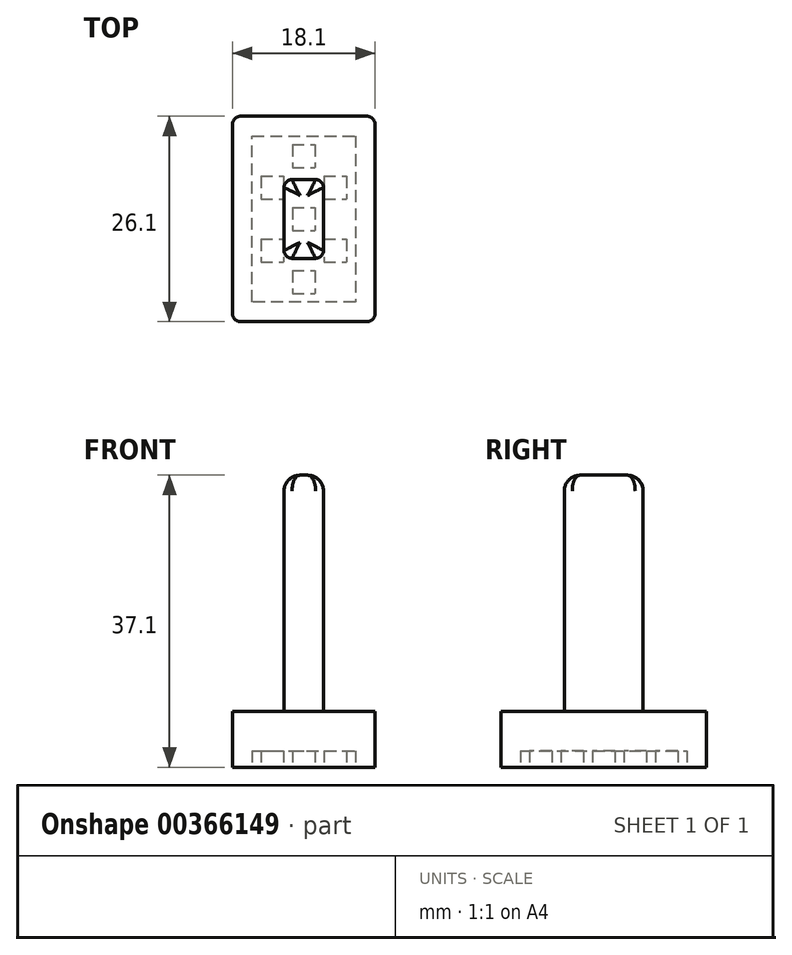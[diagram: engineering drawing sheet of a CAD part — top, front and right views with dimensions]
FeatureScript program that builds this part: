
annotation { "Feature Type Name" : "Feature", "Feature Type Description" : "" }
export const myFeature = defineFeature(function(context is Context, id is Id, definition is map)
    precondition{}
    {
        {
            var Q0;
            Q0=qCreatedBy(makeId("Top.planeOp"),FACE);
            var sketch = newSketch(context, id + "F0", { "sketchPlane" : qUnion([Q0])});
            skCircle(sketch, "E0", {"center": v(0, 0) * mm, "radius": 2.45 * mm});
            skCircle(sketch, "E1", {"center": v(0, -8) * mm, "radius": 2.45 * mm});
            skCircle(sketch, "E2", {"center": v(8, 0) * mm, "radius": 2.45 * mm});
            skCircle(sketch, "E3", {"center": v(8, -8) * mm, "radius": 2.45 * mm});
            skCircle(sketch, "E4", {"center": v(0, -16) * mm, "radius": 2.45 * mm});
            skCircle(sketch, "E5", {"center": v(8, -16) * mm, "radius": 2.45 * mm});
            skLineSegment(sketch, "E6", {"start": v(-2.55, 2.55) * mm, "end": v(10.55, 2.55) * mm});
            skLineSegment(sketch, "E7", {"start": v(10.55, 2.55) * mm, "end": v(10.55, -18.55) * mm});
            skLineSegment(sketch, "E8", {"start": v(10.55, -18.55) * mm, "end": v(-2.55, -18.55) * mm});
            skLineSegment(sketch, "E9", {"start": v(-2.55, -18.55) * mm, "end": v(-2.55, 2.55) * mm});
            skLineSegment(sketch, "E10.bottom", {"start": v(2.55, 1.45) * mm, "end": v(5.45, 1.45) * mm});
            skLineSegment(sketch, "E10.top", {"start": v(2.55, -1.45) * mm, "end": v(5.45, -1.45) * mm});
            skLineSegment(sketch, "E10.left", {"start": v(2.55, 1.45) * mm, "end": v(2.55, -1.45) * mm});
            skLineSegment(sketch, "E10.right", {"start": v(5.45, 1.45) * mm, "end": v(5.45, -1.45) * mm});
            skLineSegment(sketch, "E11.bottom", {"start": v(-1.45, -2.55) * mm, "end": v(1.45, -2.55) * mm});
            skLineSegment(sketch, "E11.top", {"start": v(-1.45, -5.45) * mm, "end": v(1.45, -5.45) * mm});
            skLineSegment(sketch, "E11.left", {"start": v(-1.45, -2.55) * mm, "end": v(-1.45, -5.45) * mm});
            skLineSegment(sketch, "E11.right", {"start": v(1.45, -2.55) * mm, "end": v(1.45, -5.45) * mm});
            skLineSegment(sketch, "E12.bottom", {"start": v(6.55, -2.55) * mm, "end": v(9.45, -2.55) * mm});
            skLineSegment(sketch, "E12.top", {"start": v(6.55, -5.45) * mm, "end": v(9.45, -5.45) * mm});
            skLineSegment(sketch, "E12.left", {"start": v(6.55, -2.55) * mm, "end": v(6.55, -5.45) * mm});
            skLineSegment(sketch, "E12.right", {"start": v(9.45, -2.55) * mm, "end": v(9.45, -5.45) * mm});
            skLineSegment(sketch, "E13.bottom", {"start": v(-1.45, -10.55) * mm, "end": v(1.45, -10.55) * mm});
            skLineSegment(sketch, "E13.top", {"start": v(-1.45, -13.45) * mm, "end": v(1.45, -13.45) * mm});
            skLineSegment(sketch, "E13.left", {"start": v(-1.45, -10.55) * mm, "end": v(-1.45, -13.45) * mm});
            skLineSegment(sketch, "E13.right", {"start": v(1.45, -10.55) * mm, "end": v(1.45, -13.45) * mm});
            skLineSegment(sketch, "E14.bottom", {"start": v(6.55, -10.55) * mm, "end": v(9.45, -10.55) * mm});
            skLineSegment(sketch, "E14.top", {"start": v(6.55, -13.45) * mm, "end": v(9.45, -13.45) * mm});
            skLineSegment(sketch, "E14.left", {"start": v(6.55, -10.55) * mm, "end": v(6.55, -13.45) * mm});
            skLineSegment(sketch, "E14.right", {"start": v(9.45, -10.55) * mm, "end": v(9.45, -13.45) * mm});
            skLineSegment(sketch, "E15.bottom", {"start": v(2.55, -14.55) * mm, "end": v(5.45, -14.55) * mm});
            skLineSegment(sketch, "E15.top", {"start": v(2.55, -17.45) * mm, "end": v(5.45, -17.45) * mm});
            skLineSegment(sketch, "E15.left", {"start": v(2.55, -14.55) * mm, "end": v(2.55, -17.45) * mm});
            skLineSegment(sketch, "E15.right", {"start": v(5.45, -14.55) * mm, "end": v(5.45, -17.45) * mm});
            skLineSegment(sketch, "E16.0", {"start": v(-5.05, 5.05) * mm, "end": v(13.05, 5.05) * mm});
            skLineSegment(sketch, "E17.0", {"start": v(-5.05, -21.05) * mm, "end": v(-5.05, 5.05) * mm});
            skLineSegment(sketch, "E18.0", {"start": v(13.05, 5.05) * mm, "end": v(13.05, -21.05) * mm});
            skLineSegment(sketch, "E19.0", {"start": v(13.05, -21.05) * mm, "end": v(-5.05, -21.05) * mm});
            skLineSegment(sketch, "E20.bottom", {"start": v(2.55, -6.55) * mm, "end": v(5.45, -6.55) * mm});
            skLineSegment(sketch, "E20.top", {"start": v(2.55, -9.45) * mm, "end": v(5.45, -9.45) * mm});
            skLineSegment(sketch, "E20.left", {"start": v(2.55, -6.55) * mm, "end": v(2.55, -9.45) * mm});
            skLineSegment(sketch, "E20.right", {"start": v(5.45, -6.55) * mm, "end": v(5.45, -9.45) * mm});
            skSolve(sketch);
        }
        {
            var Q0;
            Q0 = qSketchRegion(id + "F0", true);
            var Q1;
            Q1=makeQuery(id+"F0.imprint","IMPRINT",FACE,{"disambiguationData":[TD([[makeQuery(id+"F0.imprint","IMPRINT",EDGE,{"derivedFrom":sQuery(id+"F0.wireOp",EDGE,"E10.bottom")}),-1.0]])]});
            var Q2;
            Q2=makeQuery(id+"F0.imprint","IMPRINT",FACE,{"disambiguationData":[TD([[makeQuery(id+"F0.imprint","IMPRINT",EDGE,{"derivedFrom":sQuery(id+"F0.wireOp",EDGE,"E11.bottom")}),-1.0]])]});
            var Q3;
            Q3=makeQuery(id+"F0.imprint","IMPRINT",FACE,{"disambiguationData":[TD([[makeQuery(id+"F0.imprint","IMPRINT",EDGE,{"derivedFrom":sQuery(id+"F0.wireOp",EDGE,"E12.bottom")}),-1.0]])]});
            var Q4;
            Q4=makeQuery(id+"F0.imprint","IMPRINT",FACE,{"disambiguationData":[TD([[makeQuery(id+"F0.imprint","IMPRINT",EDGE,{"derivedFrom":sQuery(id+"F0.wireOp",EDGE,"E20.bottom")}),-1.0]])]});
            var Q5;
            Q5=makeQuery(id+"F0.imprint","IMPRINT",FACE,{"disambiguationData":[TD([[makeQuery(id+"F0.imprint","IMPRINT",EDGE,{"derivedFrom":sQuery(id+"F0.wireOp",EDGE,"E14.bottom")}),-1.0]])]});
            var Q6;
            Q6=makeQuery(id+"F0.imprint","IMPRINT",FACE,{"disambiguationData":[TD([[makeQuery(id+"F0.imprint","IMPRINT",EDGE,{"derivedFrom":sQuery(id+"F0.wireOp",EDGE,"E13.bottom")}),-1.0]])]});
            var Q7;
            Q7=makeQuery(id+"F0.imprint","IMPRINT",FACE,{"disambiguationData":[TD([[makeQuery(id+"F0.imprint","IMPRINT",EDGE,{"derivedFrom":sQuery(id+"F0.wireOp",EDGE,"E15.bottom")}),-1.0]])]});
            extrude(context, id + "F1", {"entities" : qUnion([Q0, Q1, Q2, Q3, Q4, Q5, Q6, Q7]), "depth" : 2.1 * mm});
        }
        {
            var Q0;
            Q0=makeQuery(id+"F1.opExtrude","CAP_FACE",FACE,{"disambiguationData":[OSD([sQuery(id+"F0.wireOp",EDGE,"E6"),sQuery(id+"F0.wireOp",EDGE,"E7"),sQuery(id+"F0.wireOp",EDGE,"E8"),sQuery(id+"F0.wireOp",EDGE,"E9"),sQuery(id+"F0.wireOp",EDGE,"E16.0"),sQuery(id+"F0.wireOp",EDGE,"E17.0"),sQuery(id+"F0.wireOp",EDGE,"E18.0"),sQuery(id+"F0.wireOp",EDGE,"E19.0")])],"isStart":false});
            var sketch = newSketch(context, id + "F2", { "sketchPlane" : qUnion([Q0])});
            skLineSegment(sketch, "E21.bottom", {"start": v(-5.05, 5.05) * mm, "end": v(13.05, 5.05) * mm});
            skLineSegment(sketch, "E21.top", {"start": v(-5.05, -21.05) * mm, "end": v(13.05, -21.05) * mm});
            skLineSegment(sketch, "E21.left", {"start": v(-5.05, 5.05) * mm, "end": v(-5.05, -21.05) * mm});
            skLineSegment(sketch, "E21.right", {"start": v(13.05, 5.05) * mm, "end": v(13.05, -21.05) * mm});
            skSolve(sketch);
        }
        {
            var Q0;
            Q0 = qSketchRegion(id + "F2", true);
            extrude(context, id + "F3", {"entities" : qUnion([Q0]), "depth" : 5 * mm});
        }
        {
            var Q0;
            Q0=makeQuery(id+"F3.opExtrude","SWEPT_BODY",BODY,{"disambiguationData":[OSD([sQuery(id+"F2.wireOp",EDGE,"E21.bottom"),sQuery(id+"F2.wireOp",EDGE,"E21.top"),sQuery(id+"F2.wireOp",EDGE,"E21.left"),sQuery(id+"F2.wireOp",EDGE,"E21.right")])]});
            var Q1;
            Q1=makeQuery(id+"F1.opExtrude","SWEPT_BODY",BODY,{"disambiguationData":[OSD([sQuery(id+"F0.wireOp",EDGE,"E15.bottom"),sQuery(id+"F0.wireOp",EDGE,"E15.top"),sQuery(id+"F0.wireOp",EDGE,"E15.left"),sQuery(id+"F0.wireOp",EDGE,"E15.right")])]});
            var Q2;
            Q2=makeQuery(id+"F1.opExtrude","SWEPT_BODY",BODY,{"disambiguationData":[OSD([sQuery(id+"F0.wireOp",EDGE,"E6"),sQuery(id+"F0.wireOp",EDGE,"E7"),sQuery(id+"F0.wireOp",EDGE,"E8"),sQuery(id+"F0.wireOp",EDGE,"E9"),sQuery(id+"F0.wireOp",EDGE,"E16.0"),sQuery(id+"F0.wireOp",EDGE,"E17.0"),sQuery(id+"F0.wireOp",EDGE,"E18.0"),sQuery(id+"F0.wireOp",EDGE,"E19.0")])]});
            var Q3;
            Q3=makeQuery(id+"F1.opExtrude","SWEPT_BODY",BODY,{"disambiguationData":[OSD([sQuery(id+"F0.wireOp",EDGE,"E12.bottom"),sQuery(id+"F0.wireOp",EDGE,"E12.top"),sQuery(id+"F0.wireOp",EDGE,"E12.left"),sQuery(id+"F0.wireOp",EDGE,"E12.right")])]});
            var Q4;
            Q4=makeQuery(id+"F1.opExtrude","SWEPT_BODY",BODY,{"disambiguationData":[OSD([sQuery(id+"F0.wireOp",EDGE,"E13.bottom"),sQuery(id+"F0.wireOp",EDGE,"E13.top"),sQuery(id+"F0.wireOp",EDGE,"E13.left"),sQuery(id+"F0.wireOp",EDGE,"E13.right")])]});
            var Q5;
            Q5=makeQuery(id+"F1.opExtrude","SWEPT_BODY",BODY,{"disambiguationData":[OSD([sQuery(id+"F0.wireOp",EDGE,"E10.bottom"),sQuery(id+"F0.wireOp",EDGE,"E10.top"),sQuery(id+"F0.wireOp",EDGE,"E10.left"),sQuery(id+"F0.wireOp",EDGE,"E10.right")])]});
            var Q6;
            Q6=makeQuery(id+"F1.opExtrude","SWEPT_BODY",BODY,{"disambiguationData":[OSD([sQuery(id+"F0.wireOp",EDGE,"E14.bottom"),sQuery(id+"F0.wireOp",EDGE,"E14.top"),sQuery(id+"F0.wireOp",EDGE,"E14.left"),sQuery(id+"F0.wireOp",EDGE,"E14.right")])]});
            var Q7;
            Q7=makeQuery(id+"F1.opExtrude","SWEPT_BODY",BODY,{"disambiguationData":[OSD([sQuery(id+"F0.wireOp",EDGE,"E11.bottom"),sQuery(id+"F0.wireOp",EDGE,"E11.top"),sQuery(id+"F0.wireOp",EDGE,"E11.left"),sQuery(id+"F0.wireOp",EDGE,"E11.right")])]});
            var Q8;
            Q8=makeQuery(id+"F1.opExtrude","SWEPT_BODY",BODY,{"disambiguationData":[OSD([sQuery(id+"F0.wireOp",EDGE,"E20.bottom"),sQuery(id+"F0.wireOp",EDGE,"E20.top"),sQuery(id+"F0.wireOp",EDGE,"E20.left"),sQuery(id+"F0.wireOp",EDGE,"E20.right")])]});
            booleanBodies(context, id + "F4", {"operationType" : BooleanOperationType.UNION, "tools" : qUnion([Q0, Q1, Q2, Q3, Q4, Q5, Q6, Q7, Q8])});
        }
        {
            var Q0;
            Q0=makeQuery(id+"F3.opExtrude","CAP_FACE",FACE,{"disambiguationData":[OSD([sQuery(id+"F2.wireOp",EDGE,"E21.bottom"),sQuery(id+"F2.wireOp",EDGE,"E21.top"),sQuery(id+"F2.wireOp",EDGE,"E21.left"),sQuery(id+"F2.wireOp",EDGE,"E21.right")])],"isStart":false});
            var sketch = newSketch(context, id + "F5", { "sketchPlane" : qUnion([Q0])});
            skLineSegment(sketch, "E22.bottom", {"start": v(1.5, -3) * mm, "end": v(6.5, -3) * mm});
            skLineSegment(sketch, "E22.top", {"start": v(1.5, -13) * mm, "end": v(6.5, -13) * mm});
            skLineSegment(sketch, "E22.left", {"start": v(1.5, -3) * mm, "end": v(1.5, -13) * mm});
            skLineSegment(sketch, "E22.right", {"start": v(6.5, -3) * mm, "end": v(6.5, -13) * mm});
            skLineSegment(sketch, "E23", {"start": v(4, -3) * mm, "end": v(4, 5.05) * mm, "construction": true});
            skLineSegment(sketch, "E24", {"start": v(4, -13) * mm, "end": v(4, -21.05) * mm, "construction": true});
            skLineSegment(sketch, "E25", {"start": v(1.5, -8) * mm, "end": v(-5.05, -8) * mm, "construction": true});
            skLineSegment(sketch, "E26", {"start": v(6.5, -8) * mm, "end": v(13.05, -8) * mm, "construction": true});
            skSolve(sketch);
        }
        {
            var Q0;
            Q0 = qSketchRegion(id + "F5", true);
            extrude(context, id + "F6", {"entities" : qUnion([Q0]), "operationType" : NewBodyOperationType.ADD, "depth" : 30 * mm});
        }
        {
            var Q0;
            Q0=makeQuery(id+"F6.opExtrude","CAP_FACE",FACE,{"disambiguationData":[OSD([sQuery(id+"F5.wireOp",EDGE,"E22.bottom"),sQuery(id+"F5.wireOp",EDGE,"E22.top"),sQuery(id+"F5.wireOp",EDGE,"E22.left"),sQuery(id+"F5.wireOp",EDGE,"E22.right")])],"isStart":false});
            fillet(context, id + "F7", {"entities" : qUnion([Q0]), "radius" : 2 * mm, "tangentPropagation" : true, "allowEdgeOverflow" : false});
        }
        {
            var Q0;
            Q0=makeQuery(id+"F4.opBoolean","MERGE",EDGE,{"derivedFrom":[makeQuery(id+"F1.opExtrude","SWEPT_EDGE",EDGE,{"disambiguationData":[OSD([sQuery(id+"F0.wireOp",EDGE,"E16.0"),sQuery(id+"F0.wireOp",EDGE,"E17.0")])]}),makeQuery(id+"F3.opExtrude","SWEPT_EDGE",EDGE,{"disambiguationData":[OSD([sQuery(id+"F2.wireOp",EDGE,"E21.bottom"),sQuery(id+"F2.wireOp",EDGE,"E21.left")])]})]});
            var Q1;
            Q1=makeQuery(id+"F4.opBoolean","MERGE",EDGE,{"derivedFrom":[makeQuery(id+"F1.opExtrude","SWEPT_EDGE",EDGE,{"disambiguationData":[OSD([sQuery(id+"F0.wireOp",EDGE,"E17.0"),sQuery(id+"F0.wireOp",EDGE,"E19.0")])]}),makeQuery(id+"F3.opExtrude","SWEPT_EDGE",EDGE,{"disambiguationData":[OSD([sQuery(id+"F2.wireOp",EDGE,"E21.top"),sQuery(id+"F2.wireOp",EDGE,"E21.left")])]})]});
            var Q2;
            Q2=makeQuery(id+"F4.opBoolean","MERGE",EDGE,{"derivedFrom":[makeQuery(id+"F1.opExtrude","SWEPT_EDGE",EDGE,{"disambiguationData":[OSD([sQuery(id+"F0.wireOp",EDGE,"E18.0"),sQuery(id+"F0.wireOp",EDGE,"E19.0")])]}),makeQuery(id+"F3.opExtrude","SWEPT_EDGE",EDGE,{"disambiguationData":[OSD([sQuery(id+"F2.wireOp",EDGE,"E21.top"),sQuery(id+"F2.wireOp",EDGE,"E21.right")])]})]});
            var Q3;
            Q3=makeQuery(id+"F4.opBoolean","MERGE",EDGE,{"derivedFrom":[makeQuery(id+"F1.opExtrude","SWEPT_EDGE",EDGE,{"disambiguationData":[OSD([sQuery(id+"F0.wireOp",EDGE,"E16.0"),sQuery(id+"F0.wireOp",EDGE,"E18.0")])]}),makeQuery(id+"F3.opExtrude","SWEPT_EDGE",EDGE,{"disambiguationData":[OSD([sQuery(id+"F2.wireOp",EDGE,"E21.bottom"),sQuery(id+"F2.wireOp",EDGE,"E21.right")])]})]});
            fillet(context, id + "F8", {"entities" : qUnion([Q0, Q1, Q2, Q3]), "radius" : 1 * mm, "tangentPropagation" : true, "allowEdgeOverflow" : false});
        }
        {
            var Q0;
            Q0=makeQuery(id+"F6.opExtrude","SWEPT_EDGE",EDGE,{"disambiguationData":[OSD([sQuery(id+"F5.wireOp",EDGE,"E22.bottom"),sQuery(id+"F5.wireOp",EDGE,"E22.left")])]});
            var Q1;
            Q1=makeQuery(id+"F6.opExtrude","SWEPT_EDGE",EDGE,{"disambiguationData":[OSD([sQuery(id+"F5.wireOp",EDGE,"E22.top"),sQuery(id+"F5.wireOp",EDGE,"E22.left")])]});
            var Q2;
            Q2=makeQuery(id+"F6.opExtrude","SWEPT_EDGE",EDGE,{"disambiguationData":[OSD([sQuery(id+"F5.wireOp",EDGE,"E22.top"),sQuery(id+"F5.wireOp",EDGE,"E22.right")])]});
            var Q3;
            Q3=makeQuery(id+"F6.opExtrude","SWEPT_EDGE",EDGE,{"disambiguationData":[OSD([sQuery(id+"F5.wireOp",EDGE,"E22.bottom"),sQuery(id+"F5.wireOp",EDGE,"E22.right")])]});
            fillet(context, id + "F9", {"entities" : qUnion([Q0, Q1, Q2, Q3]), "radius" : 1 * mm, "tangentPropagation" : true, "allowEdgeOverflow" : false});
        }
    });
